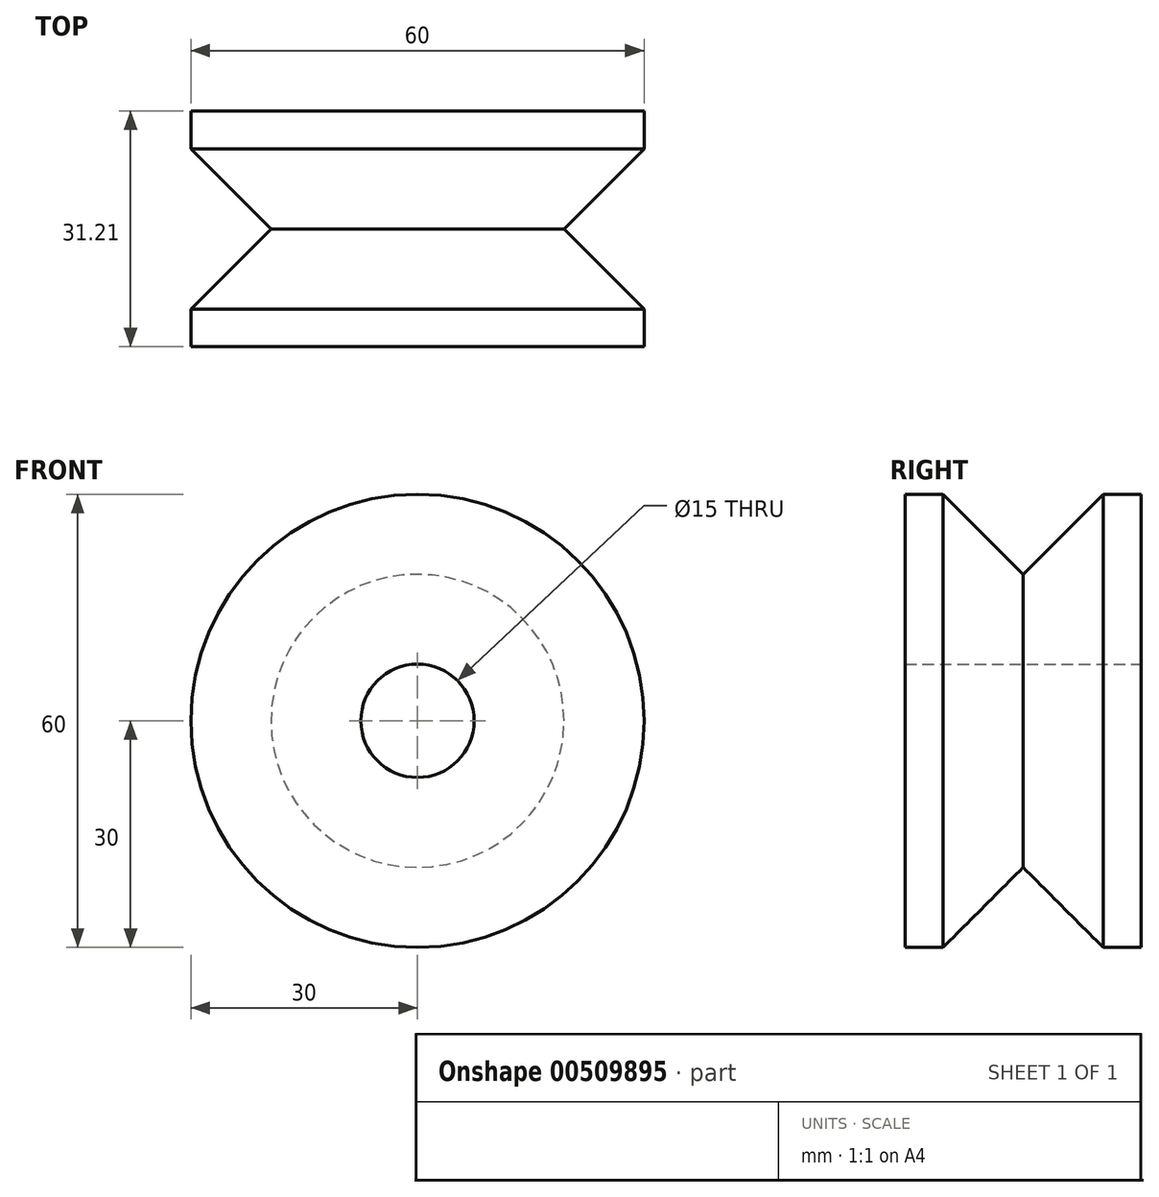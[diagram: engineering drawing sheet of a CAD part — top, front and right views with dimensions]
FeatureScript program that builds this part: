
annotation { "Feature Type Name" : "Feature", "Feature Type Description" : "" }
export const myFeature = defineFeature(function(context is Context, id is Id, definition is map)
    precondition{}
    {
        {
            var Q0;
            Q0=qCreatedBy(makeId("Right.planeOp"),FACE);
            var sketch = newSketch(context, id + "F0", { "sketchPlane" : qUnion([Q0])});
            skLineSegment(sketch, "E0", {"start": v(0, 0) * mm, "end": v(0, 30) * mm});
            skLineSegment(sketch, "E1", {"start": v(0, 30) * mm, "end": v(-5, 30) * mm});
            skLineSegment(sketch, "E2", {"start": v(-5, 30) * mm, "end": v(-15.6, 19.4) * mm});
            skLineSegment(sketch, "E3", {"start": v(-15.6, 19.4) * mm, "end": v(-26.21, 30) * mm});
            skLineSegment(sketch, "E4", {"start": v(-26.21, 30) * mm, "end": v(-31.21, 30) * mm});
            skLineSegment(sketch, "E5", {"start": v(-31.21, 30) * mm, "end": v(-31.21, 0) * mm});
            skLineSegment(sketch, "E6", {"start": v(-31.21, 0) * mm, "end": v(0, 0) * mm});
            skSolve(sketch);
        }
        {
            var Q0;
            Q0=makeQuery(id+"F0.imprint","IMPRINT",FACE,{"disambiguationData":[TD([[makeQuery(id+"F0.imprint","IMPRINT",EDGE,{"derivedFrom":sQuery(id+"F0.wireOp",EDGE,"E0")}),1.0]])]});
            var Q1;
            Q1=sQuery(id+"F0.wireOp",EDGE,"E6");
            revolve(context, id + "F1", {"entities" : qUnion([Q0]), "axis" : qUnion([Q1]), "revolveType" : RevolveType.FULL});
        }
        {
            var Q0;
            Q0=qCreatedBy(makeId("Front.planeOp"),FACE);
            var sketch = newSketch(context, id + "F2", { "sketchPlane" : qUnion([Q0])});
            skCircle(sketch, "E7", {"center": v(0, 0) * mm, "radius": 7.5 * mm});
            skSolve(sketch);
        }
        {
            var Q0;
            Q0=sQuery(id+"F2.wireOp",VERTEX,"E7.center");
            var Q1;
            Q1=makeQuery(id+"F1.opRevolve","SWEPT_BODY",BODY,{"disambiguationData":[OSD([sQuery(id+"F0.wireOp",EDGE,"E0"),sQuery(id+"F0.wireOp",EDGE,"E1"),sQuery(id+"F0.wireOp",EDGE,"E2"),sQuery(id+"F0.wireOp",EDGE,"E3"),sQuery(id+"F0.wireOp",EDGE,"E4"),sQuery(id+"F0.wireOp",EDGE,"E5"),sQuery(id+"F0.wireOp",EDGE,"E6")])]});
            hole(context, id + "F3", {"style" : HoleStyle.SIMPLE, "endStyle" : HoleEndStyle.THROUGH, "oppositeDirection" : true, "holeDiameter" : 15 * mm, "isTappedThrough" : true, "tappedDepth" : 12 * mm, "tapClearance" : 3, "locations" : qUnion([Q0]), "scope" : qUnion([Q1])});
        }
    });
